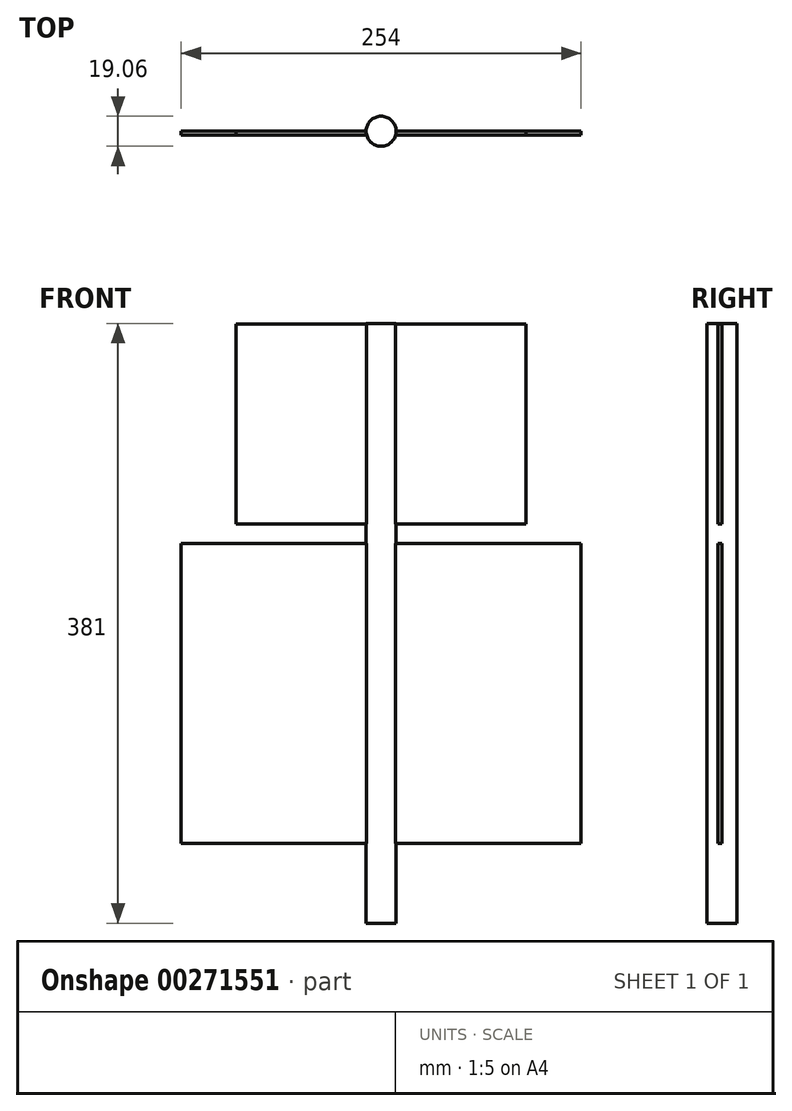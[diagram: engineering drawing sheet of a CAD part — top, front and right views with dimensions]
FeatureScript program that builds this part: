
annotation { "Feature Type Name" : "Feature", "Feature Type Description" : "" }
export const myFeature = defineFeature(function(context is Context, id is Id, definition is map)
    precondition{}
    {
        {
            var Q0;
            Q0=qCreatedBy(makeId("Front.planeOp"),FACE);
            var sketch = newSketch(context, id + "F0", { "sketchPlane" : qUnion([Q0])});
            skLineSegment(sketch, "E0", {"start": v(0, -129.55) * mm, "end": v(0, 251.45) * mm});
            skLineSegment(sketch, "E1", {"start": v(0, 251.45) * mm, "end": v(9.52, 251.45) * mm});
            skLineSegment(sketch, "E2", {"start": v(9.52, 251.45) * mm, "end": v(9.53, -129.55) * mm});
            skLineSegment(sketch, "E3", {"start": v(9.53, -129.55) * mm, "end": v(0, -129.55) * mm});
            skSolve(sketch);
        }
        {
            var Q0;
            Q0=makeQuery(id+"F0.imprint","IMPRINT",FACE,{"disambiguationData":[TD([[makeQuery(id+"F0.imprint","IMPRINT",EDGE,{"derivedFrom":sQuery(id+"F0.wireOp",EDGE,"E0")}),-1.0]])]});
            var Q1;
            Q1=sQuery(id+"F0.wireOp",EDGE,"E0");
            revolve(context, id + "F1", {"entities" : qUnion([Q0]), "axis" : qUnion([Q1]), "revolveType" : RevolveType.FULL});
        }
        {
            var Q0;
            Q0=qCreatedBy(makeId("Front.planeOp"),FACE);
            var sketch = newSketch(context, id + "F2", { "sketchPlane" : qUnion([Q0])});
            skLineSegment(sketch, "E4.bottom", {"start": v(-127, 111.75) * mm, "end": v(127, 111.75) * mm});
            skLineSegment(sketch, "E4.top", {"start": v(-127, -78.75) * mm, "end": v(127, -78.75) * mm});
            skLineSegment(sketch, "E4.left", {"start": v(-127, 111.75) * mm, "end": v(-127, -78.75) * mm});
            skLineSegment(sketch, "E4.right", {"start": v(127, 111.75) * mm, "end": v(127, -78.75) * mm});
            skPoint(sketch, "E4.middle", {"position": v(0, 16.5) * mm});
            skLineSegment(sketch, "E5.bottom", {"start": v(-92.08, 251.03) * mm, "end": v(92.08, 251.03) * mm});
            skLineSegment(sketch, "E5.top", {"start": v(-92.08, 124.03) * mm, "end": v(92.08, 124.03) * mm});
            skLineSegment(sketch, "E5.left", {"start": v(-92.08, 251.03) * mm, "end": v(-92.08, 124.03) * mm});
            skLineSegment(sketch, "E5.right", {"start": v(92.07, 251.03) * mm, "end": v(92.07, 124.03) * mm});
            skPoint(sketch, "E5.middle", {"position": v(0, 187.53) * mm});
            skSolve(sketch);
        }
        {
            var Q0;
            Q0=makeQuery(id+"F2.imprint","IMPRINT",FACE,{"disambiguationData":[TD([[makeQuery(id+"F2.imprint","IMPRINT",EDGE,{"derivedFrom":sQuery(id+"F2.wireOp",EDGE,"E5.bottom")}),-1.0]])]});
            var Q1;
            Q1=makeQuery(id+"F2.imprint","IMPRINT",FACE,{"disambiguationData":[TD([[makeQuery(id+"F2.imprint","IMPRINT",EDGE,{"derivedFrom":sQuery(id+"F2.wireOp",EDGE,"E4.bottom")}),-1.0]])]});
            extrude(context, id + "F3", {"entities" : qUnion([Q0, Q1]), "operationType" : NewBodyOperationType.ADD, "depth" : 2.54 * mm});
        }
    });
